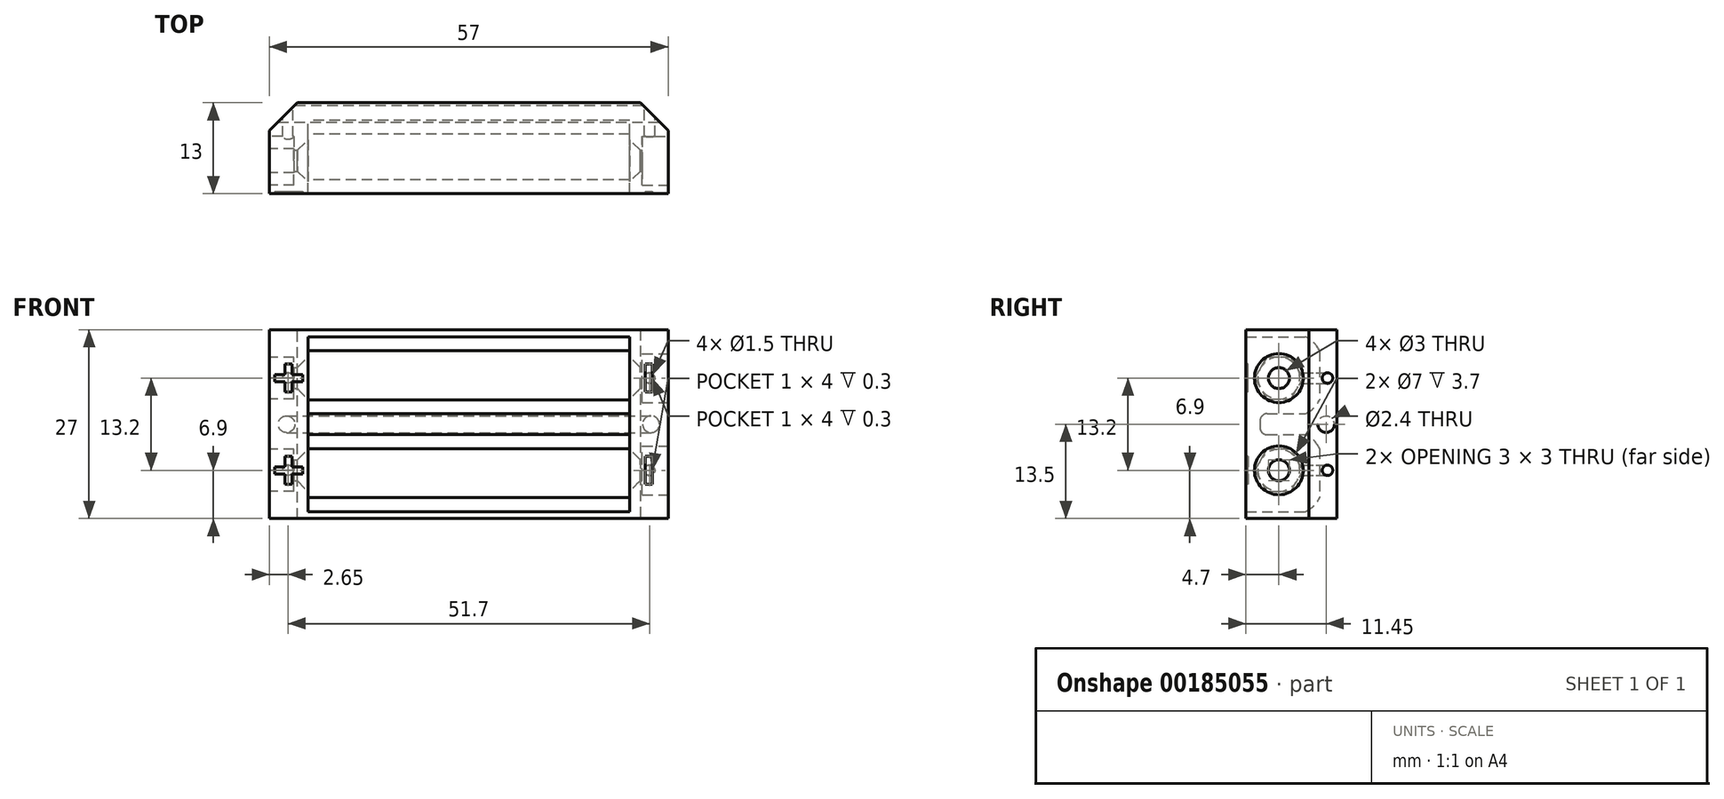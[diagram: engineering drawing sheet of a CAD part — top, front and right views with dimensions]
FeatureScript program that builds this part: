
annotation { "Feature Type Name" : "Feature", "Feature Type Description" : "" }
export const myFeature = defineFeature(function(context is Context, id is Id, definition is map)
    precondition{}
    {
        {
            var Q0;
            Q0=qCreatedBy(makeId("Front.planeOp"),FACE);
            var sketch = newSketch(context, id + "F0", { "sketchPlane" : qUnion([Q0])});
            skLineSegment(sketch, "E0.bottom", {"start": v(-28.5, -13.5) * mm, "end": v(28.5, -13.5) * mm});
            skLineSegment(sketch, "E0.top", {"start": v(-28.5, 13.5) * mm, "end": v(28.5, 13.5) * mm});
            skLineSegment(sketch, "E0.left", {"start": v(-28.5, -13.5) * mm, "end": v(-28.5, 13.5) * mm});
            skLineSegment(sketch, "E0.right", {"start": v(28.5, -13.5) * mm, "end": v(28.5, 13.5) * mm});
            skLineSegment(sketch, "E1.bottom", {"start": v(-23, 12.5) * mm, "end": v(23, 12.5) * mm});
            skLineSegment(sketch, "E1.top", {"start": v(-23, -12.5) * mm, "end": v(23, -12.5) * mm});
            skLineSegment(sketch, "E1.left", {"start": v(23, 12.5) * mm, "end": v(23, -12.5) * mm});
            skLineSegment(sketch, "E1.right", {"start": v(-23, 12.5) * mm, "end": v(-23, -12.5) * mm});
            skLineSegment(sketch, "E2", {"start": v(-14.44, 0) * mm, "end": v(20.22, 0) * mm, "construction": true});
            skLineSegment(sketch, "E3", {"start": v(0, 16.14) * mm, "end": v(0, -13.64) * mm, "construction": true});
            skLineSegment(sketch, "E4.bottom", {"start": v(-22.03, 11.7) * mm, "end": v(22.17, 11.7) * mm, "construction": true});
            skLineSegment(sketch, "E4.top", {"start": v(-22.03, 1.5) * mm, "end": v(22.17, 1.5) * mm, "construction": true});
            skLineSegment(sketch, "E4.left", {"start": v(-22.03, 11.7) * mm, "end": v(-22.03, 1.5) * mm, "construction": true});
            skLineSegment(sketch, "E4.right", {"start": v(22.17, 11.7) * mm, "end": v(22.17, 1.5) * mm, "construction": true});
            skLineSegment(sketch, "E5.bottom", {"start": v(22.01, -1.5) * mm, "end": v(-22.19, -1.5) * mm, "construction": true});
            skLineSegment(sketch, "E5.top", {"start": v(22.01, -11.7) * mm, "end": v(-22.19, -11.7) * mm, "construction": true});
            skLineSegment(sketch, "E5.left", {"start": v(22.01, -1.5) * mm, "end": v(22.01, -11.7) * mm, "construction": true});
            skLineSegment(sketch, "E5.right", {"start": v(-22.19, -1.5) * mm, "end": v(-22.19, -11.7) * mm, "construction": true});
            skSolve(sketch);
        }
        {
            var Q0;
            Q0=makeQuery(id+"F0.imprint","IMPRINT",FACE,{"disambiguationData":[TD([[makeQuery(id+"F0.imprint","IMPRINT",EDGE,{"derivedFrom":sQuery(id+"F0.wireOp",EDGE,"E0.bottom")}),1.0]])]});
            extrude(context, id + "F1", {"entities" : qUnion([Q0]), "depth" : 13 * mm});
        }
        {
            var Q0;
            Q0=makeQuery(id+"F0.imprint","IMPRINT",FACE,{"disambiguationData":[TD([[makeQuery(id+"F0.imprint","IMPRINT",EDGE,{"derivedFrom":sQuery(id+"F0.wireOp",EDGE,"E1.bottom")}),-1.0]])]});
            extrude(context, id + "F2", {"entities" : qUnion([Q0]), "operationType" : NewBodyOperationType.ADD, "depth" : 2.5 * mm});
        }
        {
            var Q0;
            Q0=makeQuery(id+"F1.opExtrude","SWEPT_FACE",FACE,{"disambiguationData":[OSD([sQuery(id+"F0.wireOp",EDGE,"E1.right")])]});
            var sketch = newSketch(context, id + "F3", { "sketchPlane" : qUnion([Q0])});
            skLineSegment(sketch, "E6.bottom", {"start": v(-11, 1.5) * mm, "end": v(-1, 1.5) * mm});
            skLineSegment(sketch, "E6.top", {"start": v(-11, -1.5) * mm, "end": v(-1, -1.5) * mm});
            skLineSegment(sketch, "E6.left", {"start": v(-11, 1.5) * mm, "end": v(-11, -1.5) * mm});
            skLineSegment(sketch, "E6.right", {"start": v(-1, 1.5) * mm, "end": v(-1, -1.5) * mm});
            skLineSegment(sketch, "E7", {"start": v(-18.91, 0) * mm, "end": v(-6.43, 0) * mm, "construction": true});
            skSolve(sketch);
        }
        {
            var Q0;
            Q0 = qSketchRegion(id + "F3", true);
            extrude(context, id + "F4", {"entities" : qUnion([Q0]), "operationType" : NewBodyOperationType.ADD, "endBound" : BoundingType.UP_TO_NEXT, "depth" : 25 * mm});
        }
        {
            var Q0;
            Q0=makeQuery(id+"F1.opExtrude","SWEPT_FACE",FACE,{"disambiguationData":[OSD([sQuery(id+"F0.wireOp",EDGE,"E1.right")])]});
            var sketch = newSketch(context, id + "F5", { "sketchPlane" : qUnion([Q0])});
            skCircle(sketch, "E8", {"center": v(-8.3, 6.6) * mm, "radius": 1.5 * mm});
            skCircle(sketch, "E9", {"center": v(-8.3, -6.6) * mm, "radius": 1.5 * mm});
            skLineSegment(sketch, "E10", {"start": v(-13, 0) * mm, "end": v(-12.09, 0) * mm, "construction": true});
            skPoint(sketch, "E11", {"position": v(-11, 0) * mm});
            skSolve(sketch);
        }
        {
            var Q0;
            Q0=makeQuery(id+"F5.imprint","IMPRINT",FACE,{"disambiguationData":[TD([[makeQuery(id+"F5.imprint","IMPRINT",EDGE,{"derivedFrom":sQuery(id+"F5.wireOp",EDGE,"E8")}),1.0]])]});
            var Q1;
            Q1=makeQuery(id+"F5.imprint","IMPRINT",FACE,{"disambiguationData":[TD([[makeQuery(id+"F5.imprint","IMPRINT",EDGE,{"derivedFrom":sQuery(id+"F5.wireOp",EDGE,"E9")}),1.0]])]});
            extrude(context, id + "F6", {"entities" : qUnion([Q0, Q1]), "operationType" : NewBodyOperationType.REMOVE, "endBound" : BoundingType.THROUGH_ALL, "oppositeDirection" : true, "depth" : 25 * mm, "hasSecondDirection" : true, "secondDirectionBound" : SecondDirectionBoundingType.THROUGH_ALL, "secondDirectionOppositeDirection" : false, "secondDirectionDepth" : 25 * mm});
        }
        {
            var Q0;
            Q0=makeQuery(id+"F6.boolean.opBoolean","INTERSECT",EDGE,{"derivedFrom":[makeQuery(id+"F1.opExtrude","SWEPT_FACE",FACE,{"disambiguationData":[OSD([sQuery(id+"F0.wireOp",EDGE,"E1.right")])]}),makeQuery(id+"F6.opExtrude","SWEPT_FACE",FACE,{"disambiguationData":[OSD([sQuery(id+"F5.wireOp",EDGE,"E8")])]})]});
            var Q1;
            Q1=makeQuery(id+"F6.boolean.opBoolean","INTERSECT",EDGE,{"derivedFrom":[makeQuery(id+"F1.opExtrude","SWEPT_FACE",FACE,{"disambiguationData":[OSD([sQuery(id+"F0.wireOp",EDGE,"E1.right")])]}),makeQuery(id+"F6.opExtrude","SWEPT_FACE",FACE,{"disambiguationData":[OSD([sQuery(id+"F5.wireOp",EDGE,"E9")])]})]});
            var Q2;
            Q2=makeQuery(id+"F6.boolean.opBoolean","INTERSECT",EDGE,{"derivedFrom":[makeQuery(id+"F1.opExtrude","SWEPT_FACE",FACE,{"disambiguationData":[OSD([sQuery(id+"F0.wireOp",EDGE,"E1.left")])]}),makeQuery(id+"F6.opExtrude","SWEPT_FACE",FACE,{"disambiguationData":[OSD([sQuery(id+"F5.wireOp",EDGE,"E8")])]})]});
            var Q3;
            Q3=makeQuery(id+"F6.boolean.opBoolean","INTERSECT",EDGE,{"derivedFrom":[makeQuery(id+"F1.opExtrude","SWEPT_FACE",FACE,{"disambiguationData":[OSD([sQuery(id+"F0.wireOp",EDGE,"E1.left")])]}),makeQuery(id+"F6.opExtrude","SWEPT_FACE",FACE,{"disambiguationData":[OSD([sQuery(id+"F5.wireOp",EDGE,"E9")])]})]});
            chamfer(context, id + "F7", {"entities" : qUnion([Q0, Q1, Q2, Q3]), "width" : 1.5 * mm, "tangentPropagation" : true});
        }
        {
            var Q0;
            Q0=makeQuery(id+"F1.opExtrude","SWEPT_FACE",FACE,{"disambiguationData":[OSD([sQuery(id+"F0.wireOp",EDGE,"E0.left")])]});
            var sketch = newSketch(context, id + "F8", { "sketchPlane" : qUnion([Q0])});
            skCircle(sketch, "E12.cCircle", {"center": v(8.3, 6.6) * mm, "radius": 3 * mm, "construction": true});
            skLineSegment(sketch, "E12.0", {"start": v(6.57, 9.6) * mm, "end": v(10.03, 9.6) * mm});
            skLineSegment(sketch, "E12.1", {"start": v(10.03, 9.6) * mm, "end": v(11.76, 6.6) * mm});
            skLineSegment(sketch, "E12.2", {"start": v(11.76, 6.6) * mm, "end": v(10.03, 3.6) * mm});
            skLineSegment(sketch, "E12.3", {"start": v(10.03, 3.6) * mm, "end": v(6.57, 3.6) * mm});
            skLineSegment(sketch, "E12.4", {"start": v(6.57, 3.6) * mm, "end": v(4.84, 6.6) * mm});
            skLineSegment(sketch, "E12.5", {"start": v(4.84, 6.6) * mm, "end": v(6.57, 9.6) * mm});
            skPoint(sketch, "E12.0.midPoint", {"position": v(8.3, 9.6) * mm});
            skCircle(sketch, "E13.cCircle", {"center": v(8.3, -6.6) * mm, "radius": 3 * mm, "construction": true});
            skLineSegment(sketch, "E13.0", {"start": v(4.84, -6.6) * mm, "end": v(6.57, -3.6) * mm});
            skLineSegment(sketch, "E13.1", {"start": v(6.57, -3.6) * mm, "end": v(10.03, -3.6) * mm});
            skLineSegment(sketch, "E13.2", {"start": v(10.03, -3.6) * mm, "end": v(11.76, -6.6) * mm});
            skLineSegment(sketch, "E13.3", {"start": v(11.76, -6.6) * mm, "end": v(10.03, -9.6) * mm});
            skLineSegment(sketch, "E13.4", {"start": v(10.03, -9.6) * mm, "end": v(6.57, -9.6) * mm});
            skLineSegment(sketch, "E13.5", {"start": v(6.57, -9.6) * mm, "end": v(4.84, -6.6) * mm});
            skPoint(sketch, "E13.0.midPoint", {"position": v(5.7, -5.1) * mm});
            skSolve(sketch);
        }
        {
            var Q0;
            Q0=makeQuery(id+"F8.imprint","IMPRINT",FACE,{"disambiguationData":[TD([[makeQuery(id+"F8.imprint","IMPRINT",EDGE,{"derivedFrom":sQuery(id+"F8.wireOp",EDGE,"E13.0")}),-1.0]])]});
            var Q1;
            Q1=makeQuery(id+"F8.imprint","IMPRINT",FACE,{"disambiguationData":[TD([[makeQuery(id+"F8.imprint","IMPRINT",EDGE,{"derivedFrom":makeQuery(id+"F6.boolean.opBoolean","INTERSECT",EDGE,{"derivedFrom":[makeQuery(id+"F1.opExtrude","SWEPT_FACE",FACE,{"disambiguationData":[OSD([sQuery(id+"F0.wireOp",EDGE,"E0.left")])]}),makeQuery(id+"F6.opExtrude","SWEPT_FACE",FACE,{"disambiguationData":[OSD([sQuery(id+"F5.wireOp",EDGE,"E8")])]})]})}),1.0]])]});
            var Q2;
            Q2=makeQuery(id+"F8.imprint","IMPRINT",FACE,{"disambiguationData":[TD([[makeQuery(id+"F8.imprint","IMPRINT",EDGE,{"derivedFrom":sQuery(id+"F8.wireOp",EDGE,"E12.0")}),-1.0]])]});
            extrude(context, id + "F9", {"entities" : qUnion([Q0, Q1, Q2]), "operationType" : NewBodyOperationType.REMOVE, "oppositeDirection" : true, "depth" : 3.5 * mm});
        }
        {
            var Q0;
            Q0=makeQuery(id+"F1.opExtrude","SWEPT_FACE",FACE,{"disambiguationData":[OSD([sQuery(id+"F0.wireOp",EDGE,"E0.right")])]});
            var sketch = newSketch(context, id + "F10", { "sketchPlane" : qUnion([Q0])});
            skCircle(sketch, "E14", {"center": v(-8.3, 6.6) * mm, "radius": 3.5 * mm});
            skCircle(sketch, "E15", {"center": v(-8.3, -6.6) * mm, "radius": 3.5 * mm});
            skSolve(sketch);
        }
        {
            var Q0;
            Q0=makeQuery(id+"F10.imprint","IMPRINT",FACE,{"disambiguationData":[TD([[makeQuery(id+"F10.imprint","IMPRINT",EDGE,{"derivedFrom":sQuery(id+"F10.wireOp",EDGE,"E14")}),1.0]])]});
            var Q1;
            Q1=makeQuery(id+"F10.imprint","IMPRINT",FACE,{"disambiguationData":[TD([[makeQuery(id+"F10.imprint","IMPRINT",EDGE,{"derivedFrom":sQuery(id+"F10.wireOp",EDGE,"E15")}),1.0]])]});
            extrude(context, id + "F11", {"entities" : qUnion([Q0, Q1]), "operationType" : NewBodyOperationType.REMOVE, "oppositeDirection" : true, "depth" : 3.7 * mm});
        }
        {
            var Q0;
            Q0=makeQuery(id+"F1.opExtrude","SWEPT_FACE",FACE,{"disambiguationData":[OSD([sQuery(id+"F0.wireOp",EDGE,"E1.right")])]});
            var sketch = newSketch(context, id + "F12", { "sketchPlane" : qUnion([Q0])});
            skLineSegment(sketch, "E16", {"start": v(-12.2, 0) * mm, "end": v(-13, 0) * mm, "construction": true});
            skPoint(sketch, "E17.endSnap0", {"position": v(-4.5, -1.5) * mm});
            skPoint(sketch, "E18", {"position": v(-4.5, 0) * mm});
            skPoint(sketch, "E19", {"position": v(-2.5, -3.5) * mm});
            skPoint(sketch, "E20", {"position": v(-2.5, 3.5) * mm});
            skArc(sketch, "E21", {"start": v(-2.5, -3.5) * mm, "mid": v(-3.32, -2.32) * mm, "end": v(-4.5, -1.5) * mm});
            skArc(sketch, "E22", {"start": v(-4.5, 1.5) * mm, "mid": v(-3.32, 2.32) * mm, "end": v(-2.5, 3.5) * mm});
            skArc(sketch, "E23", {"start": v(-2.5, 10.5) * mm, "mid": v(-3.32, 11.68) * mm, "end": v(-4.5, 12.5) * mm});
            skArc(sketch, "E24", {"start": v(-4.5, -12.5) * mm, "mid": v(-3.32, -11.68) * mm, "end": v(-2.5, -10.5) * mm});
            skPoint(sketch, "E25", {"position": v(-11, 0) * mm});
            skSolve(sketch);
        }
        {
            var Q0;
            {var subQ0=sQuery(id+"F12.wireOp",EDGE,"E24");Q0=makeQuery(id+"F12.imprint","IMPRINT",FACE,{"disambiguationData":[TD([[makeQuery(id+"F12.imprint","IMPRINT",EDGE,{"derivedFrom":subQ0}),-1.0]])]});}
            var Q1;
            {var subQ0=sQuery(id+"F12.wireOp",EDGE,"E21");Q1=makeQuery(id+"F12.imprint","IMPRINT",FACE,{"disambiguationData":[TD([[makeQuery(id+"F12.imprint","IMPRINT",EDGE,{"derivedFrom":subQ0}),-1.0]])]});}
            var Q2;
            {var subQ0=sQuery(id+"F12.wireOp",EDGE,"E23");Q2=makeQuery(id+"F12.imprint","IMPRINT",FACE,{"disambiguationData":[TD([[makeQuery(id+"F12.imprint","IMPRINT",EDGE,{"derivedFrom":subQ0}),-1.0]])]});}
            var Q3;
            {var subQ0=sQuery(id+"F12.wireOp",EDGE,"E22");Q3=makeQuery(id+"F12.imprint","IMPRINT",FACE,{"disambiguationData":[TD([[makeQuery(id+"F12.imprint","IMPRINT",EDGE,{"derivedFrom":subQ0}),-1.0]])]});}
            extrude(context, id + "F13", {"entities" : qUnion([Q0, Q1, Q2, Q3]), "operationType" : NewBodyOperationType.ADD, "endBound" : BoundingType.UP_TO_NEXT, "depth" : 25 * mm});
        }
        {
            var Q0;
            Q0=makeQuery(id+"F1.opExtrude","SWEPT_FACE",FACE,{"disambiguationData":[OSD([sQuery(id+"F0.wireOp",EDGE,"E0.right")])]});
            var sketch = newSketch(context, id + "F14", { "sketchPlane" : qUnion([Q0])});
            skCircle(sketch, "E26", {"center": v(-1.55, 0) * mm, "radius": 1.2 * mm});
            skPoint(sketch, "E26.centerSnap0", {"position": v(0, 0) * mm});
            skSolve(sketch);
        }
        {
            var Q0;
            Q0 = qSketchRegion(id + "F14", true);
            extrude(context, id + "F15", {"entities" : qUnion([Q0]), "operationType" : NewBodyOperationType.REMOVE, "endBound" : BoundingType.THROUGH_ALL, "oppositeDirection" : true, "depth" : 25 * mm});
        }
        {
            var Q0;
            {var subQ0=sQuery(id+"F0.wireOp",EDGE,"E1.right");var subQ1=sQuery(id+"F0.wireOp",EDGE,"E1.left");var subQ2=sQuery(id+"F0.wireOp",EDGE,"E1.top");var subQ3=sQuery(id+"F0.wireOp",EDGE,"E1.bottom");Q0=makeQuery(id+"F2.boolean.opBoolean","MERGE",FACE,{"derivedFrom":[makeQuery(id+"F1.opExtrude","CAP_FACE",FACE,{"disambiguationData":[OSD([sQuery(id+"F0.wireOp",EDGE,"E0.bottom"),sQuery(id+"F0.wireOp",EDGE,"E0.top"),sQuery(id+"F0.wireOp",EDGE,"E0.left"),sQuery(id+"F0.wireOp",EDGE,"E0.right"),subQ3,subQ2,subQ1,subQ0])],"isStart":true}),makeQuery(id+"F2.opExtrude","CAP_FACE",FACE,{"disambiguationData":[OSD([subQ3,subQ2,subQ1,subQ0])],"isStart":true})]});}
            var sketch = newSketch(context, id + "F16", { "sketchPlane" : qUnion([Q0])});
            skCircle(sketch, "E27", {"center": v(-25.85, -6.6) * mm, "radius": 0.75 * mm});
            skCircle(sketch, "E28", {"center": v(-25.85, 6.6) * mm, "radius": 0.75 * mm});
            skCircle(sketch, "E29", {"center": v(25.85, 6.6) * mm, "radius": 0.75 * mm});
            skCircle(sketch, "E30", {"center": v(25.85, -6.6) * mm, "radius": 0.75 * mm});
            skLineSegment(sketch, "E31", {"start": v(-28.5, 0) * mm, "end": v(28.5, 0) * mm, "construction": true});
            skLineSegment(sketch, "E32", {"start": v(0, -13.5) * mm, "end": v(0, 13.5) * mm, "construction": true});
            skSolve(sketch);
        }
        {
            var Q0;
            Q0 = qSketchRegion(id + "F16", true);
            extrude(context, id + "F17", {"entities" : qUnion([Q0]), "operationType" : NewBodyOperationType.REMOVE, "oppositeDirection" : true, "depth" : 6 * mm});
        }
        {
            var Q0;
            Q0=makeQuery(id+"F1.opExtrude","CAP_EDGE",EDGE,{"disambiguationData":[OSD([sQuery(id+"F0.wireOp",EDGE,"E0.right")])],"isStart":true});
            var Q1;
            Q1=makeQuery(id+"F1.opExtrude","CAP_EDGE",EDGE,{"disambiguationData":[OSD([sQuery(id+"F0.wireOp",EDGE,"E0.left")])],"isStart":true});
            chamfer(context, id + "F18", {"entities" : qUnion([Q0, Q1]), "width" : 4 * mm, "tangentPropagation" : true});
        }
        {
            var Q0;
            Q0=makeQuery(id+"F1.opExtrude","CAP_FACE",FACE,{"disambiguationData":[OSD([sQuery(id+"F0.wireOp",EDGE,"E0.bottom"),sQuery(id+"F0.wireOp",EDGE,"E0.top"),sQuery(id+"F0.wireOp",EDGE,"E0.left"),sQuery(id+"F0.wireOp",EDGE,"E0.right"),sQuery(id+"F0.wireOp",EDGE,"E1.bottom"),sQuery(id+"F0.wireOp",EDGE,"E1.top"),sQuery(id+"F0.wireOp",EDGE,"E1.left"),sQuery(id+"F0.wireOp",EDGE,"E1.right")])],"isStart":false});
            var sketch = newSketch(context, id + "F19", { "sketchPlane" : qUnion([Q0])});
            skLineSegment(sketch, "E33.bottom", {"start": v(25.25, -8.6) * mm, "end": v(26.25, -8.6) * mm});
            skLineSegment(sketch, "E33.top", {"start": v(25.25, -4.6) * mm, "end": v(26.25, -4.6) * mm});
            skLineSegment(sketch, "E33.left", {"start": v(25.25, -8.6) * mm, "end": v(25.25, -4.6) * mm});
            skLineSegment(sketch, "E33.right", {"start": v(26.25, -8.6) * mm, "end": v(26.25, -4.6) * mm});
            skLineSegment(sketch, "E34.bottom", {"start": v(25.25, 4.6) * mm, "end": v(26.25, 4.6) * mm});
            skLineSegment(sketch, "E34.top", {"start": v(25.25, 8.6) * mm, "end": v(26.25, 8.6) * mm});
            skLineSegment(sketch, "E34.left", {"start": v(25.25, 4.6) * mm, "end": v(25.25, 8.6) * mm});
            skLineSegment(sketch, "E34.right", {"start": v(26.25, 4.6) * mm, "end": v(26.25, 8.6) * mm});
            skLineSegment(sketch, "E35.bottom", {"start": v(-26.25, 4.6) * mm, "end": v(-25.25, 4.6) * mm});
            skLineSegment(sketch, "E35.top", {"start": v(-26.25, 8.6) * mm, "end": v(-25.25, 8.6) * mm});
            skLineSegment(sketch, "E35.left", {"start": v(-26.25, 4.6) * mm, "end": v(-26.25, 8.6) * mm});
            skLineSegment(sketch, "E35.right", {"start": v(-25.25, 4.6) * mm, "end": v(-25.25, 8.6) * mm});
            skLineSegment(sketch, "E36.bottom", {"start": v(-25.25, -4.6) * mm, "end": v(-26.25, -4.6) * mm});
            skLineSegment(sketch, "E36.top", {"start": v(-25.25, -8.6) * mm, "end": v(-26.25, -8.6) * mm});
            skLineSegment(sketch, "E36.left", {"start": v(-25.25, -4.6) * mm, "end": v(-25.25, -8.6) * mm});
            skLineSegment(sketch, "E36.right", {"start": v(-26.25, -4.6) * mm, "end": v(-26.25, -8.6) * mm});
            skLineSegment(sketch, "E37.bottom", {"start": v(-27.75, -7.1) * mm, "end": v(-23.75, -7.1) * mm});
            skLineSegment(sketch, "E37.top", {"start": v(-27.75, -6.1) * mm, "end": v(-23.75, -6.1) * mm});
            skLineSegment(sketch, "E37.left", {"start": v(-27.75, -7.1) * mm, "end": v(-27.75, -6.1) * mm});
            skLineSegment(sketch, "E37.right", {"start": v(-23.75, -7.1) * mm, "end": v(-23.75, -6.1) * mm});
            skLineSegment(sketch, "E38.bottom", {"start": v(-27.75, 6.1) * mm, "end": v(-23.75, 6.1) * mm});
            skLineSegment(sketch, "E38.top", {"start": v(-27.75, 7.1) * mm, "end": v(-23.75, 7.1) * mm});
            skLineSegment(sketch, "E38.left", {"start": v(-27.75, 6.1) * mm, "end": v(-27.75, 7.1) * mm});
            skLineSegment(sketch, "E38.right", {"start": v(-23.75, 6.1) * mm, "end": v(-23.75, 7.1) * mm});
            skLineSegment(sketch, "E39", {"start": v(-27.75, -6.6) * mm, "end": v(-23.75, -6.6) * mm, "construction": true});
            skLineSegment(sketch, "E40", {"start": v(-25.75, -8.6) * mm, "end": v(-25.75, -4.6) * mm, "construction": true});
            skLineSegment(sketch, "E41", {"start": v(-23, -12.5) * mm, "end": v(-28.5, -12.5) * mm, "construction": true});
            skLineSegment(sketch, "E42", {"start": v(-25.75, -12.5) * mm, "end": v(-25.75, 12.85) * mm, "construction": true});
            skLineSegment(sketch, "E43", {"start": v(23, -12.5) * mm, "end": v(28.5, -12.5) * mm, "construction": true});
            skLineSegment(sketch, "E44", {"start": v(25.75, -12.5) * mm, "end": v(25.75, 11.2) * mm, "construction": true});
            skLineSegment(sketch, "E45", {"start": v(-27.75, 6.6) * mm, "end": v(-23.75, 6.6) * mm, "construction": true});
            skLineSegment(sketch, "E46", {"start": v(28.5, 0) * mm, "end": v(-28.5, 0) * mm, "construction": true});
            skSolve(sketch);
        }
        {
            var Q0;
            Q0 = qSketchRegion(id + "F19", true);
            extrude(context, id + "F20", {"entities" : qUnion([Q0]), "operationType" : NewBodyOperationType.REMOVE, "oppositeDirection" : true, "depth" : 0.3 * mm});
        }
        {
            var Q0;
            Q0=makeQuery(id+"F4.opExtrude","SWEPT_EDGE",EDGE,{"disambiguationData":[OSD([sQuery(id+"F3.wireOp",EDGE,"E6.top"),sQuery(id+"F3.wireOp",EDGE,"E6.left")])]});
            var Q1;
            Q1=makeQuery(id+"F4.opExtrude","SWEPT_EDGE",EDGE,{"disambiguationData":[OSD([sQuery(id+"F3.wireOp",EDGE,"E6.bottom"),sQuery(id+"F3.wireOp",EDGE,"E6.left")])]});
            fillet(context, id + "F21", {"entities" : qUnion([Q0, Q1]), "radius" : 1 * mm, "tangentPropagation" : true, "allowEdgeOverflow" : false});
        }
    });
